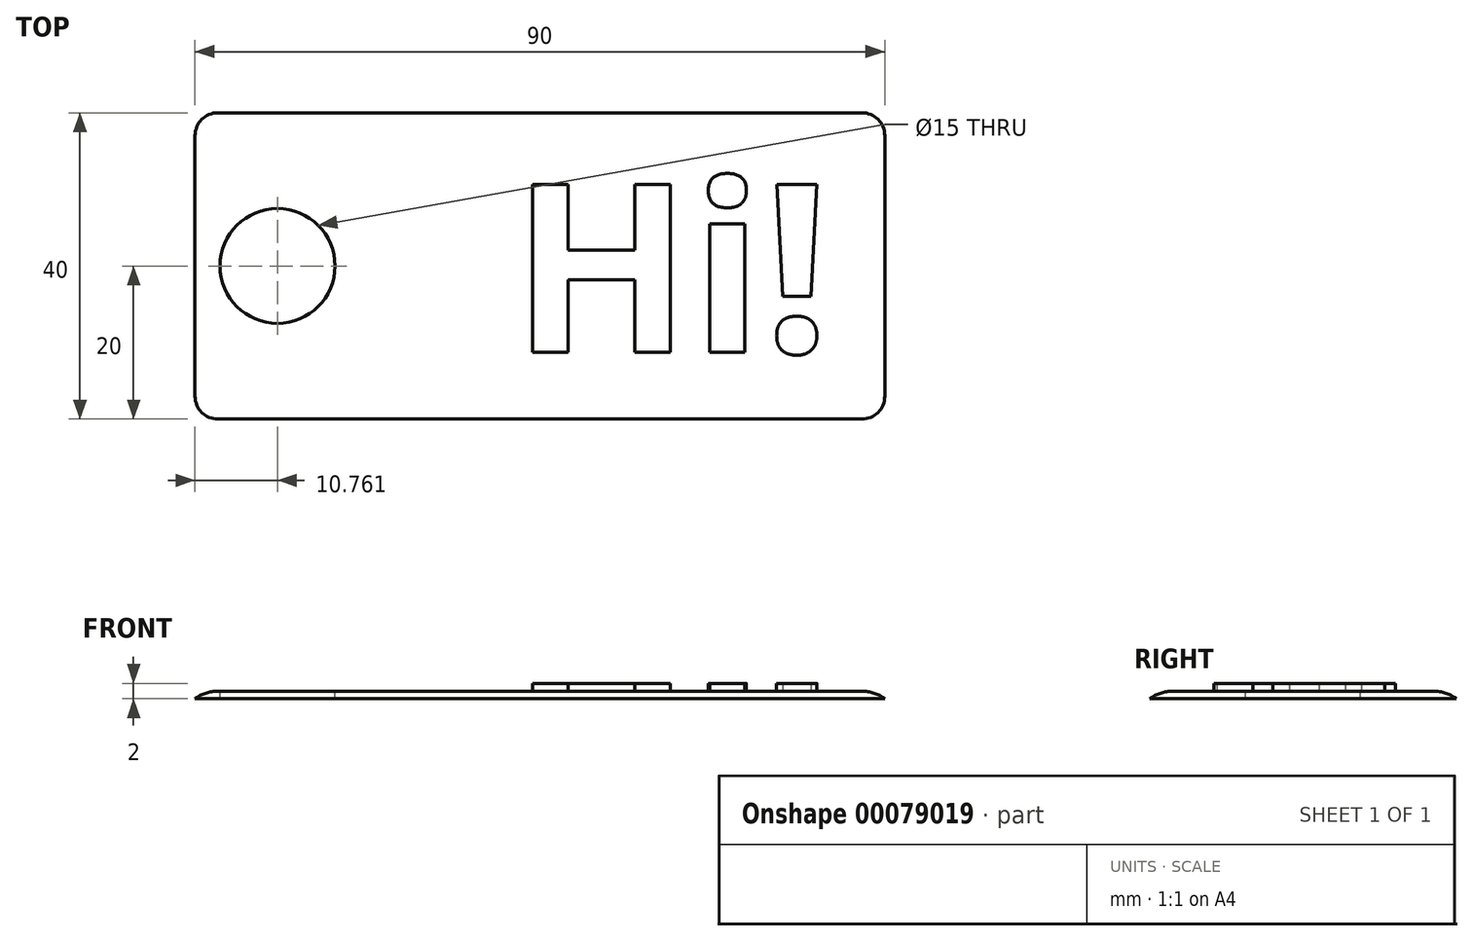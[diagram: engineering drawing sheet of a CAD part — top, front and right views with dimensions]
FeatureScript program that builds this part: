
annotation { "Feature Type Name" : "Feature", "Feature Type Description" : "" }
export const myFeature = defineFeature(function(context is Context, id is Id, definition is map)
    precondition{}
    {
        {
            var Q0;
            Q0=qCreatedBy(makeId("Top.planeOp"),FACE);
            var sketch = newSketch(context, id + "F0", { "sketchPlane" : qUnion([Q0])});
            skLineSegment(sketch, "E0.bottom", {"start": v(-45, 20) * mm, "end": v(45, 20) * mm});
            skLineSegment(sketch, "E0.top", {"start": v(-45, -20) * mm, "end": v(45, -20) * mm});
            skLineSegment(sketch, "E0.left", {"start": v(-45, 20) * mm, "end": v(-45, -20) * mm});
            skLineSegment(sketch, "E0.right", {"start": v(45, 20) * mm, "end": v(45, -20) * mm});
            skPoint(sketch, "E0.middle", {"position": v(0, 0) * mm});
            skSolve(sketch);
        }
        {
            var Q0;
            Q0 = qSketchRegion(id + "F0", true);
            extrude(context, id + "F1", {"entities" : qUnion([Q0]), "depth" : 1 * mm});
        }
        {
            var Q0;
            Q0=makeQuery(id+"F1.opExtrude","CAP_FACE",FACE,{"disambiguationData":[OSD([sQuery(id+"F0.wireOp",EDGE,"E0.bottom"),sQuery(id+"F0.wireOp",EDGE,"E0.top"),sQuery(id+"F0.wireOp",EDGE,"E0.left"),sQuery(id+"F0.wireOp",EDGE,"E0.right")])],"isStart":false});
            var sketch = newSketch(context, id + "F2", { "sketchPlane" : qUnion([Q0])});
            skText(sketch, "E1", { "text": "Hi!", "fontName": "OpenSans-Bold.ttf"});
            const initialGuessF2  = {"E1": [-0.00372, -0.01125, 1, 0, 0.0221]};
            skSetInitialGuess(sketch, initialGuessF2);
            skSolve(sketch);
        }
        {
            var Q0;
            Q0 = qSketchRegion(id + "F2", true);
            extrude(context, id + "F3", {"entities" : qUnion([Q0]), "operationType" : NewBodyOperationType.ADD, "depth" : 1 * mm});
        }
        {
            var Q0;
            Q0=makeQuery(id+"F1.opExtrude","CAP_FACE",FACE,{"disambiguationData":[OSD([sQuery(id+"F0.wireOp",EDGE,"E0.bottom"),sQuery(id+"F0.wireOp",EDGE,"E0.top"),sQuery(id+"F0.wireOp",EDGE,"E0.left"),sQuery(id+"F0.wireOp",EDGE,"E0.right")])],"isStart":false});
            var sketch = newSketch(context, id + "F4", { "sketchPlane" : qUnion([Q0])});
            skPoint(sketch, "E2", {"position": v(-34.24, 0) * mm});
            skSolve(sketch);
        }
        {
            var Q0;
            Q0=sQuery(id+"F4.wireOp",VERTEX,"E2");
            var Q1;
            Q1=makeQuery(id+"F1.opExtrude","SWEPT_BODY",BODY,{"disambiguationData":[OSD([sQuery(id+"F0.wireOp",EDGE,"E0.bottom"),sQuery(id+"F0.wireOp",EDGE,"E0.top"),sQuery(id+"F0.wireOp",EDGE,"E0.left"),sQuery(id+"F0.wireOp",EDGE,"E0.right")])]});
            hole(context, id + "F5", {"style" : HoleStyle.SIMPLE, "endStyle" : HoleEndStyle.BLIND, "holeDiameter" : 15 * mm, "holeDepth" : 50 * mm, "locations" : qUnion([Q0]), "scope" : qUnion([Q1])});
        }
        {
            var Q0;
            Q0=makeQuery(id+"F1.opExtrude","CAP_EDGE",EDGE,{"disambiguationData":[OSD([sQuery(id+"F0.wireOp",EDGE,"E0.bottom")])],"isStart":false});
            var Q1;
            Q1=makeQuery(id+"F1.opExtrude","CAP_EDGE",EDGE,{"disambiguationData":[OSD([sQuery(id+"F0.wireOp",EDGE,"E0.left")])],"isStart":false});
            var Q2;
            Q2=makeQuery(id+"F1.opExtrude","CAP_EDGE",EDGE,{"disambiguationData":[OSD([sQuery(id+"F0.wireOp",EDGE,"E0.top")])],"isStart":false});
            var Q3;
            Q3=makeQuery(id+"F1.opExtrude","CAP_EDGE",EDGE,{"disambiguationData":[OSD([sQuery(id+"F0.wireOp",EDGE,"E0.right")])],"isStart":false});
            fillet(context, id + "F6", {"entities" : qUnion([Q0, Q1, Q2, Q3]), "radius" : 5 * mm, "tangentPropagation" : true, "allowEdgeOverflow" : false});
        }
        {
            var Q0;
            Q0=makeQuery(id+"F6.opFillet","BLEND_EDGE",EDGE,{"blendedFrom":[makeQuery(id+"F1.opExtrude","CAP_EDGE",EDGE,{"disambiguationData":[OSD([sQuery(id+"F0.wireOp",EDGE,"E0.top")])],"isStart":false}),makeQuery(id+"F1.opExtrude","CAP_EDGE",EDGE,{"disambiguationData":[OSD([sQuery(id+"F0.wireOp",EDGE,"E0.left")])],"isStart":false})],"blendedInto":[]});
            var Q1;
            Q1=makeQuery(id+"F6.opFillet","BLEND_EDGE",EDGE,{"blendedFrom":[makeQuery(id+"F1.opExtrude","CAP_EDGE",EDGE,{"disambiguationData":[OSD([sQuery(id+"F0.wireOp",EDGE,"E0.top")])],"isStart":false}),makeQuery(id+"F1.opExtrude","CAP_EDGE",EDGE,{"disambiguationData":[OSD([sQuery(id+"F0.wireOp",EDGE,"E0.right")])],"isStart":false})],"blendedInto":[]});
            var Q2;
            Q2=makeQuery(id+"F6.opFillet","BLEND_EDGE",EDGE,{"blendedFrom":[makeQuery(id+"F1.opExtrude","CAP_EDGE",EDGE,{"disambiguationData":[OSD([sQuery(id+"F0.wireOp",EDGE,"E0.bottom")])],"isStart":false}),makeQuery(id+"F1.opExtrude","CAP_EDGE",EDGE,{"disambiguationData":[OSD([sQuery(id+"F0.wireOp",EDGE,"E0.right")])],"isStart":false})],"blendedInto":[]});
            var Q3;
            Q3=makeQuery(id+"F6.opFillet","BLEND_EDGE",EDGE,{"blendedFrom":[makeQuery(id+"F1.opExtrude","CAP_EDGE",EDGE,{"disambiguationData":[OSD([sQuery(id+"F0.wireOp",EDGE,"E0.bottom")])],"isStart":false}),makeQuery(id+"F1.opExtrude","CAP_EDGE",EDGE,{"disambiguationData":[OSD([sQuery(id+"F0.wireOp",EDGE,"E0.left")])],"isStart":false})],"blendedInto":[]});
            fillet(context, id + "F7", {"entities" : qUnion([Q0, Q1, Q2, Q3]), "radius" : 5 * mm, "tangentPropagation" : true, "allowEdgeOverflow" : false});
        }
    });
